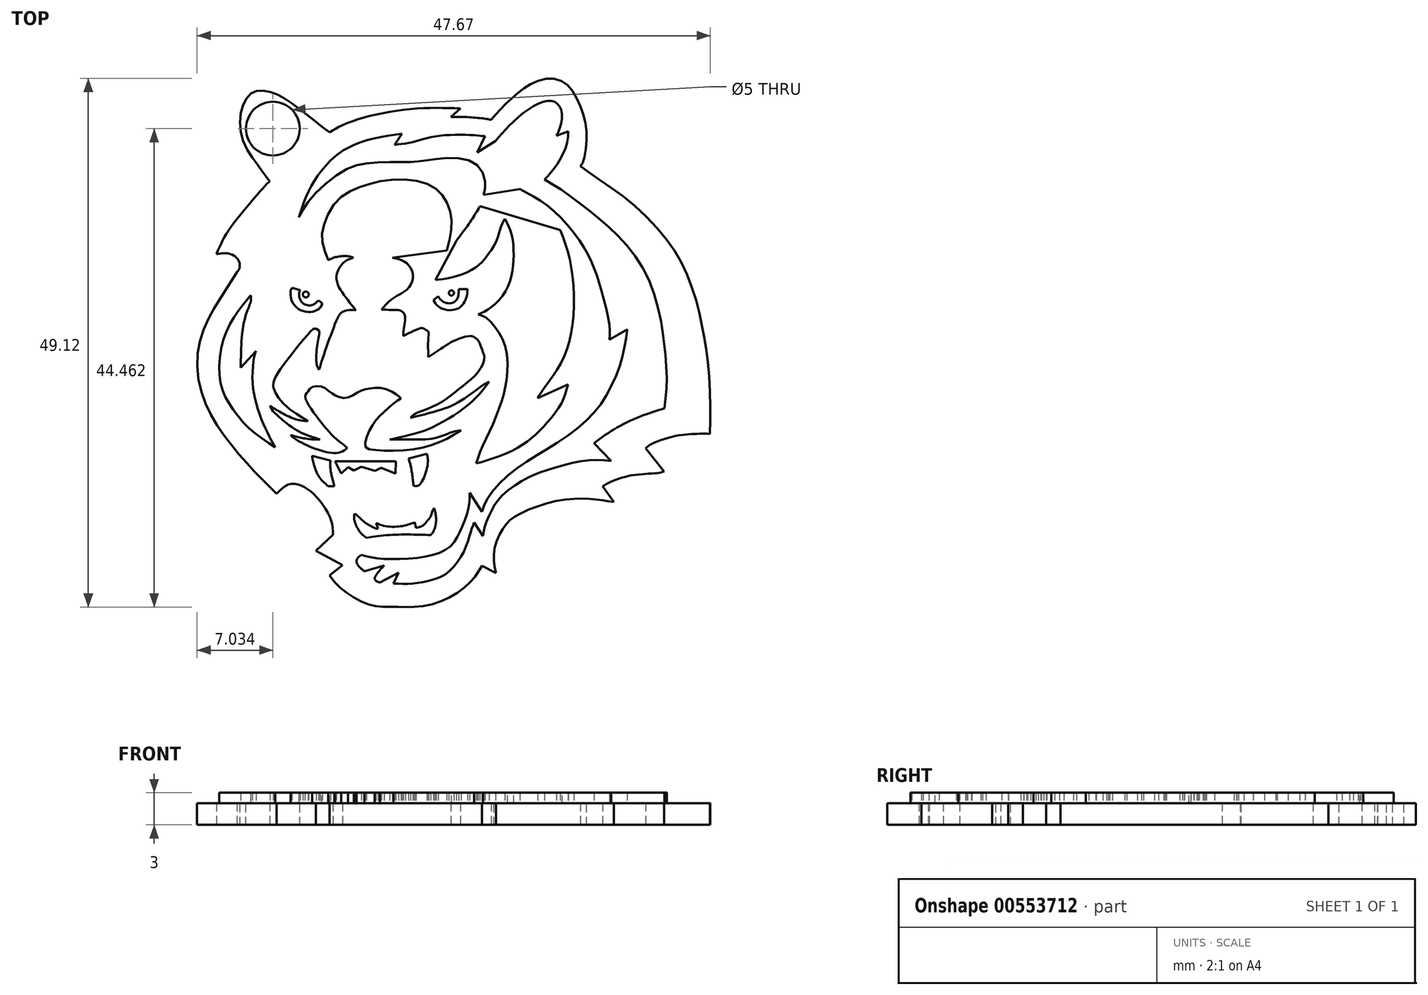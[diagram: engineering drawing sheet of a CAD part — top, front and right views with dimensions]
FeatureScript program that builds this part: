
annotation { "Feature Type Name" : "Feature", "Feature Type Description" : "" }
export const myFeature = defineFeature(function(context is Context, id is Id, definition is map)
    precondition{}
    {
        {
            var Q0;
            Q0=qCreatedBy(makeId("Top.planeOp"),FACE);
            var sketch = newSketch(context, id + "F0", { "sketchPlane" : qUnion([Q0])});
            skFitSpline(sketch, "E0", {"points": [v(7.81, 40.72) * mm, v(6.75, 42.15) * mm, v(5.2, 44.9) * mm, v(5.37, 47.9) * mm, v(6.45, 49.1) * mm, v(8.34, 48.86) * mm, v(10.63, 47.4) * mm, v(13.37, 45.26) * mm], "startDerivative": vector(-8.02, 10.82) * mm, "endDerivative": vector(16.53, -13.06) * mm});
            skFitSpline(sketch, "E1", {"points": [v(13.37, 45.26) * mm, v(14.48, 45.9) * mm, v(17.51, 46.9) * mm, v(21.92, 47.52) * mm, v(25.53, 47.5) * mm], "startDerivative": vector(5.91, 3.88) * mm, "endDerivative": vector(12.73, -0.45) * mm});
            skLineSegment(sketch, "E2", {"start": v(25.53, 47.5) * mm, "end": v(24.65, 46.7) * mm});
            skFitSpline(sketch, "E3", {"points": [v(24.65, 46.7) * mm, v(25.95, 46.7) * mm, v(27.64, 46.57) * mm, v(28.4, 46.44) * mm], "startDerivative": vector(3.55, 0.08) * mm, "endDerivative": vector(2.56, -0.49) * mm});
            skFitSpline(sketch, "E4", {"points": [v(28.4, 46.44) * mm, v(29.28, 47.45) * mm, v(30.65, 48.74) * mm, v(31.99, 49.72) * mm, v(33.8, 50.28) * mm, v(35.3, 49.8) * mm, v(36.35, 48.45) * mm, v(37.13, 46.27) * mm, v(37.24, 44.35) * mm, v(36.95, 42.59) * mm, v(36.68, 42.13) * mm], "startDerivative": vector(8.82, 10.83) * mm, "endDerivative": vector(-4.9, -6.26) * mm});
            skFitSpline(sketch, "E5", {"points": [v(36.68, 42.13) * mm, v(38.88, 40.57) * mm, v(41.72, 38.46) * mm, v(44.65, 35.36) * mm, v(46.27, 32.76) * mm, v(47.42, 29.68) * mm, v(48.02, 27.06) * mm, v(48.47, 24.4) * mm, v(48.73, 20.6) * mm, v(48.71, 17.26) * mm], "startDerivative": vector(21.07, -15.18) * mm, "endDerivative": vector(-0.6, -28.72) * mm});
            skFitSpline(sketch, "E6", {"points": [v(48.71, 17.26) * mm, v(47.43, 17.26) * mm, v(45.51, 17.05) * mm, v(43.32, 16.32) * mm, v(42.73, 15.9) * mm], "startDerivative": vector(-5.33, 0.08) * mm, "endDerivative": vector(-2.67, -2.33) * mm});
            skLineSegment(sketch, "E7", {"start": v(42.73, 15.9) * mm, "end": v(44.44, 13.75) * mm});
            skFitSpline(sketch, "E8", {"points": [v(44.44, 13.75) * mm, v(43.8, 13.6) * mm, v(41.83, 13.45) * mm, v(39.8, 12.93) * mm, v(38.74, 12.38) * mm], "startDerivative": vector(-3.21, -0.92) * mm, "endDerivative": vector(-4.23, -2.48) * mm});
            skLineSegment(sketch, "E9", {"start": v(38.74, 12.38) * mm, "end": v(39.77, 10.91) * mm});
            skFitSpline(sketch, "E10", {"points": [v(39.77, 10.91) * mm, v(38.01, 11.17) * mm, v(34.73, 11.07) * mm, v(30.8, 9.68) * mm, v(29.5, 8.5) * mm, v(28.66, 6.31) * mm, v(28.83, 4.33) * mm], "startDerivative": vector(-11.65, 2.05) * mm, "endDerivative": vector(2.66, -12.91) * mm});
            skLineSegment(sketch, "E11", {"start": v(28.83, 4.33) * mm, "end": v(27.53, 4.98) * mm});
            skFitSpline(sketch, "E12", {"points": [v(27.53, 4.98) * mm, v(26.17, 3.2) * mm, v(22.77, 1.4) * mm, v(19.43, 1.17) * mm, v(16.9, 1.44) * mm, v(14.23, 3.07) * mm, v(13.38, 4.11) * mm], "startDerivative": vector(-7.12, -11.85) * mm, "endDerivative": vector(-5.57, 8.3) * mm});
            skLineSegment(sketch, "E13", {"start": v(13.38, 4.11) * mm, "end": v(14.57, 5.06) * mm});
            skLineSegment(sketch, "E14", {"start": v(14.57, 5.06) * mm, "end": v(12.1, 6.37) * mm});
            skLineSegment(sketch, "E15", {"start": v(12.1, 6.37) * mm, "end": v(13.7, 7.88) * mm});
            skFitSpline(sketch, "E16", {"points": [v(13.7, 7.88) * mm, v(13.5, 9.24) * mm, v(12.24, 11.3) * mm, v(10.86, 12.38) * mm, v(9.66, 12.57) * mm, v(8.45, 11.69) * mm], "startDerivative": vector(-0.25, 6.98) * mm, "endDerivative": vector(-6.09, -5.97) * mm});
            skFitSpline(sketch, "E17", {"points": [v(8.45, 11.69) * mm, v(6.28, 13.88) * mm, v(3.78, 16.82) * mm, v(1.69, 20.46) * mm, v(1.15, 25) * mm, v(2.49, 28.64) * mm, v(3.74, 30.67) * mm, v(4.78, 32.28) * mm], "startDerivative": vector(-15.64, 15.32) * mm, "endDerivative": vector(9.41, 14.8) * mm});
            skFitSpline(sketch, "E18", {"points": [v(4.78, 32.28) * mm, v(5.04, 32.84) * mm, v(4.78, 33.57) * mm, v(3.95, 34.01) * mm, v(2.86, 33.96) * mm], "startDerivative": vector(1.64, 2.46) * mm, "endDerivative": vector(-3.9, -0.58) * mm});
            skFitSpline(sketch, "E19", {"points": [v(2.86, 33.96) * mm, v(3.74, 35.78) * mm, v(5.19, 37.75) * mm, v(7.28, 40.2) * mm, v(7.81, 40.72) * mm], "startDerivative": vector(3.23, 7.37) * mm, "endDerivative": vector(2.88, 2.61) * mm});
            skSolve(sketch);
        }
        {
            var Q0;
            Q0 = qSketchRegion(id + "F0", true);
            extrude(context, id + "F1", {"entities" : qUnion([Q0]), "depth" : 2 * mm, "offsetDistance" : 25 * mm});
        }
        {
            var Q0;
            Q0=makeQuery(id+"F1.opExtrude","CAP_FACE",FACE,{"disambiguationData":[OSD([sQuery(id+"F0.wireOp",EDGE,"E0"),sQuery(id+"F0.wireOp",EDGE,"E1"),sQuery(id+"F0.wireOp",EDGE,"E2"),sQuery(id+"F0.wireOp",EDGE,"E3"),sQuery(id+"F0.wireOp",EDGE,"E4"),sQuery(id+"F0.wireOp",EDGE,"E5"),sQuery(id+"F0.wireOp",EDGE,"E6"),sQuery(id+"F0.wireOp",EDGE,"E7"),sQuery(id+"F0.wireOp",EDGE,"E8"),sQuery(id+"F0.wireOp",EDGE,"E9"),sQuery(id+"F0.wireOp",EDGE,"E10"),sQuery(id+"F0.wireOp",EDGE,"E11"),sQuery(id+"F0.wireOp",EDGE,"E12"),sQuery(id+"F0.wireOp",EDGE,"E13"),sQuery(id+"F0.wireOp",EDGE,"E14"),sQuery(id+"F0.wireOp",EDGE,"E15"),sQuery(id+"F0.wireOp",EDGE,"E16"),sQuery(id+"F0.wireOp",EDGE,"E17"),sQuery(id+"F0.wireOp",EDGE,"E18"),sQuery(id+"F0.wireOp",EDGE,"E19")])],"isStart":false});
            var sketch = newSketch(context, id + "F2", { "sketchPlane" : qUnion([Q0])});
            skFitSpline(sketch, "E20", {"points": [v(10.53, 37.37) * mm, v(11.43, 39.82) * mm, v(13.3, 42.5) * mm, v(15.95, 44.25) * mm, v(20.1, 45.17) * mm], "startDerivative": vector(3.35, 10.9) * mm, "endDerivative": vector(15.52, 2.41) * mm});
            skLineSegment(sketch, "E21", {"start": v(20.1, 45.17) * mm, "end": v(19.39, 44.11) * mm});
            skFitSpline(sketch, "E22", {"points": [v(19.39, 44.11) * mm, v(21.18, 44.4) * mm, v(23.38, 44.94) * mm, v(26.66, 45.02) * mm, v(27.8, 44.92) * mm], "startDerivative": vector(7.65, 0.87) * mm, "endDerivative": vector(5.17, -0.57) * mm});
            skLineSegment(sketch, "E23", {"start": v(27.8, 44.92) * mm, "end": v(27.1, 43.4) * mm});
            skLineSegment(sketch, "E24", {"start": v(27.1, 43.4) * mm, "end": v(28.8, 44.48) * mm});
            skFitSpline(sketch, "E25", {"points": [v(28.8, 44.48) * mm, v(30.2, 46.04) * mm, v(32.48, 47.81) * mm, v(33.94, 48.2) * mm, v(34.71, 47.75) * mm, v(34.96, 46.42) * mm, v(34.45, 44.95) * mm], "startDerivative": vector(6.7, 8.1) * mm, "endDerivative": vector(-4.17, -8.84) * mm});
            skLineSegment(sketch, "E26", {"start": v(34.45, 44.95) * mm, "end": v(35.55, 45.38) * mm});
            skFitSpline(sketch, "E27", {"points": [v(35.55, 45.38) * mm, v(35.4, 44.18) * mm, v(34.5, 42.3) * mm, v(33.35, 40.9) * mm], "startDerivative": vector(-0.13, -4) * mm, "endDerivative": vector(-3.4, -3.76) * mm});
            skFitSpline(sketch, "E28", {"points": [v(33.35, 40.9) * mm, v(35.14, 39.77) * mm, v(37.76, 37.8) * mm, v(40.44, 35.37) * mm, v(42.85, 31.96) * mm, v(44.17, 27.69) * mm, v(44.55, 24.83) * mm, v(44.7, 21.88) * mm, v(44.48, 19.61) * mm], "startDerivative": vector(16.84, -9.97) * mm, "endDerivative": vector(-2.76, -20.54) * mm});
            skFitSpline(sketch, "E29", {"points": [v(44.48, 19.61) * mm, v(42.5, 18.97) * mm, v(40.03, 17.8) * mm, v(37.94, 16.4) * mm], "startDerivative": vector(-6.21, -1.84) * mm, "endDerivative": vector(-5.9, -4.31) * mm});
            skLineSegment(sketch, "E30", {"start": v(37.94, 16.4) * mm, "end": v(39.55, 14.75) * mm});
            skFitSpline(sketch, "E31", {"points": [v(39.55, 14.75) * mm, v(36.97, 14.75) * mm, v(33.68, 13.9) * mm, v(31.8, 13.18) * mm, v(29.49, 11.6) * mm, v(28.43, 10.14) * mm, v(27.8, 8.73) * mm, v(27.63, 7.76) * mm], "startDerivative": vector(-15.4, 1.2) * mm, "endDerivative": vector(-1.14, -9.47) * mm});
            skLineSegment(sketch, "E32", {"start": v(27.63, 7.76) * mm, "end": v(26.8, 9.02) * mm});
            skFitSpline(sketch, "E33", {"points": [v(26.8, 9.02) * mm, v(26.5, 8.2) * mm, v(25.9, 6.43) * mm, v(24.35, 4.37) * mm, v(22.78, 3.65) * mm, v(20.98, 3.34) * mm, v(19.3, 3.35) * mm], "startDerivative": vector(-2.47, -6.28) * mm, "endDerivative": vector(-10.06, 0.52) * mm});
            skLineSegment(sketch, "E34", {"start": v(19.3, 3.35) * mm, "end": v(19.8, 4.34) * mm});
            skLineSegment(sketch, "E35", {"start": v(19.8, 4.34) * mm, "end": v(18.02, 3.43) * mm});
            skFitSpline(sketch, "E36", {"points": [v(18.02, 3.43) * mm, v(17.66, 3.61) * mm, v(17.58, 3.88) * mm, v(18.45, 5.03) * mm], "startDerivative": vector(-1.53, 0.57) * mm, "endDerivative": vector(2.39, 2.61) * mm});
            skLineSegment(sketch, "E37", {"start": v(18.45, 5.03) * mm, "end": v(16.61, 4.49) * mm});
            skFitSpline(sketch, "E38", {"points": [v(16.61, 4.49) * mm, v(16.22, 4.81) * mm, v(15.87, 5.46) * mm, v(16.31, 6) * mm], "startDerivative": vector(-1.27, 0.92) * mm, "endDerivative": vector(1.85, 1.44) * mm});
            skFitSpline(sketch, "E39", {"points": [v(16.31, 6) * mm, v(18, 5.67) * mm, v(21.67, 5.75) * mm, v(24.4, 6.64) * mm, v(25.52, 8.24) * mm, v(26.25, 10.16) * mm, v(26.4, 11.79) * mm], "startDerivative": vector(10.26, -2.68) * mm, "endDerivative": vector(0.23, 11.3) * mm});
            skLineSegment(sketch, "E40", {"start": v(26.4, 11.79) * mm, "end": v(27.54, 10.01) * mm});
            skFitSpline(sketch, "E41", {"points": [v(27.54, 10.01) * mm, v(28.07, 11.31) * mm, v(30.5, 13.84) * mm, v(34.06, 16.13) * mm, v(37.5, 18.76) * mm, v(39.42, 21.42) * mm, v(40.62, 24.55) * mm, v(41.01, 26.96) * mm], "startDerivative": vector(3.56, 12.77) * mm, "endDerivative": vector(2.1, 18.49) * mm});
            skLineSegment(sketch, "E42", {"start": v(41.01, 26.96) * mm, "end": v(39.37, 26) * mm});
            skFitSpline(sketch, "E43", {"points": [v(39.37, 26) * mm, v(39.37, 27.44) * mm, v(38.38, 31.39) * mm, v(37.18, 34.28) * mm, v(34.1, 38.06) * mm, v(31.05, 40) * mm], "startDerivative": vector(0.9, 9.34) * mm, "endDerivative": vector(-14.64, 7.54) * mm});
            skFitSpline(sketch, "E44", {"points": [v(10.53, 37.37) * mm, v(11.64, 39.14) * mm, v(14.84, 41.79) * mm, v(17.34, 42.45) * mm, v(20.51, 42.52) * mm, v(22.04, 42.63) * mm, v(24.67, 42.9) * mm, v(27.07, 42.26) * mm, v(27.83, 40.57) * mm, v(27.68, 39.48) * mm], "startDerivative": vector(8, 15.77) * mm, "endDerivative": vector(-3.48, -13.06) * mm});
            skLineSegment(sketch, "E45", {"start": v(31.05, 40) * mm, "end": v(27.68, 39.48) * mm});
            skSolve(sketch);
        }
        {
            var Q0;
            Q0 = qSketchRegion(id + "F2", true);
            extrude(context, id + "F3", {"entities" : qUnion([Q0]), "operationType" : NewBodyOperationType.ADD, "depth" : 1 * mm, "offsetDistance" : 25 * mm});
        }
        {
            var Q0;
            Q0=makeQuery(id+"F1.opExtrude","CAP_FACE",FACE,{"disambiguationData":[OSD([sQuery(id+"F0.wireOp",EDGE,"E0"),sQuery(id+"F0.wireOp",EDGE,"E1"),sQuery(id+"F0.wireOp",EDGE,"E2"),sQuery(id+"F0.wireOp",EDGE,"E3"),sQuery(id+"F0.wireOp",EDGE,"E4"),sQuery(id+"F0.wireOp",EDGE,"E5"),sQuery(id+"F0.wireOp",EDGE,"E6"),sQuery(id+"F0.wireOp",EDGE,"E7"),sQuery(id+"F0.wireOp",EDGE,"E8"),sQuery(id+"F0.wireOp",EDGE,"E9"),sQuery(id+"F0.wireOp",EDGE,"E10"),sQuery(id+"F0.wireOp",EDGE,"E11"),sQuery(id+"F0.wireOp",EDGE,"E12"),sQuery(id+"F0.wireOp",EDGE,"E13"),sQuery(id+"F0.wireOp",EDGE,"E14"),sQuery(id+"F0.wireOp",EDGE,"E15"),sQuery(id+"F0.wireOp",EDGE,"E16"),sQuery(id+"F0.wireOp",EDGE,"E17"),sQuery(id+"F0.wireOp",EDGE,"E18"),sQuery(id+"F0.wireOp",EDGE,"E19")])],"isStart":false});
            var sketch = newSketch(context, id + "F4", { "sketchPlane" : qUnion([Q0])});
            skCircle(sketch, "E46", {"center": v(8.1, 45.62) * mm, "radius": 2.5 * mm});
            skSolve(sketch);
        }
        {
            var Q0;
            Q0 = qSketchRegion(id + "F4", true);
            extrude(context, id + "F5", {"entities" : qUnion([Q0]), "operationType" : NewBodyOperationType.REMOVE, "oppositeDirection" : true, "depth" : 9.3 * mm, "offsetDistance" : 25 * mm});
        }
        {
            var Q0;
            Q0=qCreatedBy(makeId("Top.planeOp"),FACE);
            var sketch = newSketch(context, id + "F6", { "sketchPlane" : qUnion([Q0])});
            skFitSpline(sketch, "E47", {"points": [v(13.24, 33.4) * mm, v(12.68, 35.22) * mm, v(12.9, 36.85) * mm, v(14.22, 39.08) * mm, v(16.26, 40.21) * mm, v(18.57, 40.82) * mm, v(21.75, 40.71) * mm, v(23.6, 39.73) * mm, v(24.47, 38.23) * mm, v(24.71, 36.58) * mm, v(24.27, 34.3) * mm], "startDerivative": vector(-7.82, 19.9) * mm, "endDerivative": vector(-5.93, -22.88) * mm});
            skFitSpline(sketch, "E48", {"points": [v(13.24, 33.4) * mm, v(13.75, 33.63) * mm, v(14.83, 33.8) * mm, v(15.59, 33.65) * mm], "startDerivative": vector(1.6, 0.86) * mm, "endDerivative": vector(2.13, -0.64) * mm});
            skFitSpline(sketch, "E49", {"points": [v(15.59, 33.65) * mm, v(15, 33.4) * mm, v(14.33, 32.77) * mm, v(14.01, 31.8) * mm, v(14.3, 30.8) * mm, v(15.01, 29.75) * mm, v(15.81, 28.75) * mm], "startDerivative": vector(-4.44, -1.5) * mm, "endDerivative": vector(4.26, -5.28) * mm});
            skFitSpline(sketch, "E50", {"points": [v(15.81, 28.75) * mm, v(15.14, 28.75) * mm, v(14.4, 28.45) * mm, v(13.83, 27.34) * mm, v(13.09, 25.32) * mm, v(12.4, 23.22) * mm], "startDerivative": vector(-4.6, 0.29) * mm, "endDerivative": vector(-2.56, -8.11) * mm});
            skFitSpline(sketch, "E51", {"points": [v(12.4, 23.22) * mm, v(12.21, 23.56) * mm, v(12.14, 24.15) * mm, v(12.23, 25.5) * mm, v(12.4, 26.45) * mm, v(12.4, 26.86) * mm], "startDerivative": vector(-1.43, 2.12) * mm, "endDerivative": vector(-0.16, 2.44) * mm});
            skFitSpline(sketch, "E52", {"points": [v(12.4, 26.86) * mm, v(11.97, 27.06) * mm, v(11.42, 26.58) * mm, v(10.45, 25.41) * mm, v(9.17, 23.78) * mm, v(8.43, 22.68) * mm, v(8.13, 21.72) * mm, v(9.2, 19.96) * mm, v(11.08, 18.62) * mm, v(11.36, 18.46) * mm], "startDerivative": vector(-6.12, 4.78) * mm, "endDerivative": vector(3.63, -2.2) * mm});
            skFitSpline(sketch, "E53", {"points": [v(11.36, 18.46) * mm, v(10.33, 18.58) * mm, v(8.78, 19.29) * mm, v(7.83, 19.88) * mm], "startDerivative": vector(-3.22, 0.09) * mm, "endDerivative": vector(-2.75, 1.81) * mm});
            skFitSpline(sketch, "E54", {"points": [v(7.83, 19.88) * mm, v(8.02, 19.5) * mm, v(9.4, 18.23) * mm, v(10.93, 17.27) * mm, v(12.5, 16.73) * mm], "startDerivative": vector(0.74, -2.41) * mm, "endDerivative": vector(5.78, -1.73) * mm});
            skFitSpline(sketch, "E55", {"points": [v(12.5, 16.73) * mm, v(12, 16.73) * mm, v(10.66, 16.9) * mm, v(9.75, 17.15) * mm], "startDerivative": vector(-1.73, -0.07) * mm, "endDerivative": vector(-2.4, 0.78) * mm});
            skFitSpline(sketch, "E56", {"points": [v(9.75, 17.15) * mm, v(10.06, 16.86) * mm, v(11.59, 16.05) * mm, v(13.5, 15.48) * mm, v(14.46, 15.58) * mm, v(15.01, 15.94) * mm], "startDerivative": vector(1.88, -2.12) * mm, "endDerivative": vector(3.25, 2.62) * mm});
            skFitSpline(sketch, "E57", {"points": [v(15.01, 15.94) * mm, v(14.5, 16.37) * mm, v(13.6, 17.15) * mm, v(12.1, 18.98) * mm, v(11.1, 20.72) * mm, v(11.36, 21.18) * mm], "startDerivative": vector(-3.23, 2.86) * mm, "endDerivative": vector(3.01, 2.95) * mm});
            skFitSpline(sketch, "E58", {"points": [v(11.36, 21.18) * mm, v(11.7, 21.57) * mm, v(12.62, 21.65) * mm, v(13.37, 21.18) * mm, v(14.11, 20.72) * mm, v(15.01, 20.63) * mm, v(16.15, 21.18) * mm, v(17.02, 21.46) * mm, v(18.45, 21.47) * mm, v(19.73, 20.79) * mm, v(20, 20.54) * mm], "startDerivative": vector(3.35, 5.85) * mm, "endDerivative": vector(3.17, -3.45) * mm});
            skFitSpline(sketch, "E59", {"points": [v(20, 20.54) * mm, v(19.56, 20.26) * mm, v(18.59, 19.44) * mm, v(17.83, 18.7) * mm, v(17.12, 17.64) * mm, v(16.67, 16.32) * mm, v(16.81, 15.94) * mm, v(18.1, 15.71) * mm, v(21.06, 15.8) * mm, v(23.65, 16.5) * mm, v(25.6, 17.57) * mm], "startDerivative": vector(-6.46, -3.6) * mm, "endDerivative": vector(14.8, 8.97) * mm});
            skFitSpline(sketch, "E60", {"points": [v(25.6, 17.57) * mm, v(24.85, 17.44) * mm, v(23.25, 16.88) * mm, v(21.21, 16.73) * mm, v(18.95, 16.73) * mm], "startDerivative": vector(-4.02, -0.33) * mm, "endDerivative": vector(-7.75, -0.01) * mm});
            skFitSpline(sketch, "E61", {"points": [v(18.95, 16.73) * mm, v(19.57, 16.86) * mm, v(21.39, 17.3) * mm, v(22.95, 17.89) * mm, v(25.2, 19.16) * mm, v(26.9, 20.54) * mm, v(28.2, 22.1) * mm], "startDerivative": vector(5.26, 1.04) * mm, "endDerivative": vector(6.92, 9.02) * mm});
            skFitSpline(sketch, "E62", {"points": [v(28.2, 22.1) * mm, v(27.55, 21.72) * mm, v(25.6, 20.35) * mm, v(23.78, 19.52) * mm, v(20.91, 18.75) * mm], "startDerivative": vector(-3.56, -1.81) * mm, "endDerivative": vector(-9.88, -2.45) * mm});
            skFitSpline(sketch, "E63", {"points": [v(20.91, 18.75) * mm, v(21.28, 19.08) * mm, v(23.36, 19.97) * mm, v(25.44, 21.46) * mm, v(27.2, 23.02) * mm, v(27.76, 24.31) * mm, v(27.63, 24.79) * mm], "startDerivative": vector(2.67, 3.37) * mm, "endDerivative": vector(-2.1, 4.28) * mm});
            skFitSpline(sketch, "E64", {"points": [v(27.63, 24.79) * mm, v(27.32, 25.68) * mm, v(26.72, 26.3) * mm, v(25.8, 26.23) * mm, v(24.7, 25.8) * mm, v(23.84, 25.24) * mm, v(22.54, 24.4) * mm], "startDerivative": vector(-1.62, 5.77) * mm, "endDerivative": vector(-6.9, -4.43) * mm});
            skFitSpline(sketch, "E65", {"points": [v(22.54, 24.4) * mm, v(22.54, 25.04) * mm, v(22.54, 25.97) * mm, v(22.54, 26.78) * mm, v(22.32, 26.92) * mm, v(21.98, 27.08) * mm, v(21.27, 26.86) * mm, v(20.22, 26.37) * mm], "startDerivative": vector(0.05, 4.46) * mm, "endDerivative": vector(-5.69, -2.7) * mm});
            skFitSpline(sketch, "E66", {"points": [v(20.22, 26.37) * mm, v(20.22, 26.74) * mm, v(20.36, 27.61) * mm, v(20.36, 28.28) * mm, v(19.99, 28.7) * mm, v(19.33, 28.78) * mm, v(18.19, 28.8) * mm], "startDerivative": vector(-0.17, 2.7) * mm, "endDerivative": vector(-5.67, 0.14) * mm});
            skFitSpline(sketch, "E67", {"points": [v(18.19, 28.8) * mm, v(19.3, 29.86) * mm, v(20.74, 30.85) * mm, v(21.1, 32.16) * mm, v(20.36, 33.24) * mm, v(19.22, 33.62) * mm], "startDerivative": vector(4.77, 5.48) * mm, "endDerivative": vector(-6.56, 1.2) * mm});
            skLineSegment(sketch, "E68", {"start": v(24.27, 34.3) * mm, "end": v(19.22, 33.62) * mm});
            skSolve(sketch);
        }
        {
            var Q0;
            Q0 = qSketchRegion(id + "F6", true);
            extrude(context, id + "F7", {"entities" : qUnion([Q0]), "operationType" : NewBodyOperationType.ADD, "depth" : 3 * mm, "offsetDistance" : 25 * mm});
        }
        {
            var Q0;
            Q0=qCreatedBy(makeId("Top.planeOp"),FACE);
            var sketch = newSketch(context, id + "F8", { "sketchPlane" : qUnion([Q0])});
            skLineSegment(sketch, "E69", {"start": v(11.75, 15.2) * mm, "end": v(13.46, 14.78) * mm});
            skFitSpline(sketch, "E70", {"points": [v(11.75, 15.2) * mm, v(11.88, 14.54) * mm, v(12.36, 13.32) * mm, v(13.24, 12.4) * mm], "startDerivative": vector(0.37, -2.26) * mm, "endDerivative": vector(2.65, -2.27) * mm});
            skLineSegment(sketch, "E71", {"start": v(13.24, 12.4) * mm, "end": v(13.81, 12.4) * mm});
            skFitSpline(sketch, "E72", {"points": [v(13.46, 14.78) * mm, v(13.46, 13.93) * mm, v(13.81, 12.4) * mm], "startDerivative": vector(-0.13, -1.86) * mm, "endDerivative": vector(0.79, -2.86) * mm});
            skLineSegment(sketch, "E73", {"start": v(13.88, 14.7) * mm, "end": v(19.52, 14.7) * mm});
            skLineSegment(sketch, "E74", {"start": v(13.88, 14.7) * mm, "end": v(14.46, 13.57) * mm});
            skLineSegment(sketch, "E75", {"start": v(14.46, 13.57) * mm, "end": v(15.08, 14.17) * mm});
            skLineSegment(sketch, "E76", {"start": v(15.08, 14.17) * mm, "end": v(15.62, 13.85) * mm});
            skLineSegment(sketch, "E77", {"start": v(15.62, 13.85) * mm, "end": v(16.33, 14.2) * mm});
            skLineSegment(sketch, "E78", {"start": v(16.33, 14.2) * mm, "end": v(17.58, 13.82) * mm});
            skLineSegment(sketch, "E79", {"start": v(17.58, 13.82) * mm, "end": v(18.16, 14.1) * mm});
            skLineSegment(sketch, "E80", {"start": v(18.16, 14.1) * mm, "end": v(19.49, 13.57) * mm});
            skLineSegment(sketch, "E81", {"start": v(19.49, 13.57) * mm, "end": v(19.52, 14.7) * mm});
            skLineSegment(sketch, "E82", {"start": v(20.7, 14.95) * mm, "end": v(22.44, 15.41) * mm});
            skFitSpline(sketch, "E83", {"points": [v(20.7, 14.95) * mm, v(20.93, 14.18) * mm, v(21.18, 12.43) * mm], "startDerivative": vector(0.58, -1.72) * mm, "endDerivative": vector(0.37, -3.23) * mm});
            skFitSpline(sketch, "E84", {"points": [v(21.18, 12.43) * mm, v(21.6, 12.43) * mm, v(22.08, 13.06) * mm, v(22.5, 14.5) * mm, v(22.44, 15.41) * mm], "startDerivative": vector(2.44, -0.49) * mm, "endDerivative": vector(-0.53, 3.29) * mm});
            skFitSpline(sketch, "E85", {"points": [v(15.7, 9.85) * mm, v(15.67, 9.27) * mm, v(16.17, 8.17) * mm, v(16.8, 7.58) * mm], "startDerivative": vector(-0.36, -1.91) * mm, "endDerivative": vector(1.93, -1.45) * mm});
            skFitSpline(sketch, "E86", {"points": [v(16.8, 7.58) * mm, v(17.53, 7.7) * mm, v(18.8, 7.84) * mm, v(20.16, 7.9) * mm, v(21.6, 7.88) * mm, v(22.77, 7.85) * mm], "startDerivative": vector(4.28, 0.73) * mm, "endDerivative": vector(5.74, -0.17) * mm});
            skFitSpline(sketch, "E87", {"points": [v(22.77, 7.85) * mm, v(23.07, 8.27) * mm, v(23.27, 9.41) * mm, v(23.08, 10.34) * mm], "startDerivative": vector(1.23, 1.33) * mm, "endDerivative": vector(-0.74, 2.47) * mm});
            skFitSpline(sketch, "E88", {"points": [v(23.08, 10.34) * mm, v(22.9, 10.04) * mm, v(22.78, 9.6) * mm, v(22.47, 9.2) * mm, v(22.11, 8.79) * mm, v(21.63, 8.56) * mm, v(21.4, 8.52) * mm], "startDerivative": vector(-1.4, -1.82) * mm, "endDerivative": vector(-1.68, -0.2) * mm});
            skFitSpline(sketch, "E89", {"points": [v(21.4, 8.52) * mm, v(21.27, 9.04) * mm], "startDerivative": vector(-0.13, 0.51) * mm, "endDerivative": vector(-0.13, 0.51) * mm});
            skFitSpline(sketch, "E90", {"points": [v(21.27, 9.04) * mm, v(21, 8.93) * mm, v(20.42, 8.75) * mm, v(19.96, 8.66) * mm, v(19.02, 8.62) * mm, v(18.13, 8.79) * mm, v(17.7, 8.97) * mm], "startDerivative": vector(-1.93, -0.9) * mm, "endDerivative": vector(-2.58, 1.28) * mm});
            skFitSpline(sketch, "E91", {"points": [v(17.7, 8.97) * mm, v(17.88, 8.45) * mm], "startDerivative": vector(0.17, -0.52) * mm, "endDerivative": vector(0.17, -0.52) * mm});
            skFitSpline(sketch, "E92", {"points": [v(17.88, 8.45) * mm, v(17.7, 8.45) * mm, v(17.25, 8.67) * mm, v(16.63, 9.04) * mm, v(16.04, 9.58) * mm, v(15.7, 9.85) * mm], "startDerivative": vector(-1.34, -0.22) * mm, "endDerivative": vector(-1.76, 1.26) * mm});
            skSolve(sketch);
        }
        {
            var Q0;
            Q0 = qSketchRegion(id + "F8", true);
            extrude(context, id + "F9", {"entities" : qUnion([Q0]), "operationType" : NewBodyOperationType.ADD, "depth" : 3 * mm, "offsetDistance" : 25 * mm});
        }
        {
            var Q0;
            Q0=qCreatedBy(makeId("Top.planeOp"),FACE);
            var sketch = newSketch(context, id + "F10", { "sketchPlane" : qUnion([Q0])});
            skCircle(sketch, "E93", {"center": v(11.17, 30.2) * mm, "radius": 0.27 * mm});
            skCircle(sketch, "E94", {"center": v(24.7, 30.35) * mm, "radius": 0.24 * mm});
            skLineSegment(sketch, "E95", {"start": v(9.86, 30.82) * mm, "end": v(10.63, 30.6) * mm});
            skFitSpline(sketch, "E96", {"points": [v(10.63, 30.6) * mm, v(10.54, 30.08) * mm, v(10.8, 29.5) * mm, v(11.3, 29.21) * mm, v(11.82, 29.25) * mm, v(12.34, 29.65) * mm], "startDerivative": vector(-0.82, -2.67) * mm, "endDerivative": vector(2.38, 2.29) * mm});
            skLineSegment(sketch, "E97", {"start": v(12.34, 29.65) * mm, "end": v(12.7, 29.38) * mm});
            skFitSpline(sketch, "E98", {"points": [v(9.86, 30.82) * mm, v(9.75, 30.52) * mm, v(9.86, 29.64) * mm, v(10.25, 29.04) * mm, v(10.9, 28.67) * mm, v(11.8, 28.6) * mm, v(12.41, 28.91) * mm, v(12.7, 29.38) * mm], "startDerivative": vector(-1.51, -2.47) * mm, "endDerivative": vector(1.87, 3.84) * mm});
            skLineSegment(sketch, "E99", {"start": v(25.37, 30.7) * mm, "end": v(26.18, 30.7) * mm});
            skLineSegment(sketch, "E100", {"start": v(23.46, 30.04) * mm, "end": v(23.03, 29.67) * mm});
            skFitSpline(sketch, "E101", {"points": [v(23.03, 29.67) * mm, v(23.36, 29.21) * mm, v(24.07, 28.81) * mm, v(25.1, 28.82) * mm, v(25.74, 29.27) * mm, v(26.1, 30) * mm, v(26.18, 30.7) * mm], "startDerivative": vector(1.93, -3.38) * mm, "endDerivative": vector(0.25, 4.38) * mm});
            skFitSpline(sketch, "E102", {"points": [v(23.46, 30.04) * mm, v(23.74, 29.67) * mm, v(24.13, 29.45) * mm, v(24.7, 29.4) * mm, v(25.15, 29.67) * mm, v(25.32, 30.04) * mm, v(25.37, 30.7) * mm], "startDerivative": vector(1.67, -2.47) * mm, "endDerivative": vector(0.08, 3.7) * mm});
            skSolve(sketch);
        }
        {
            var Q0;
            Q0 = qSketchRegion(id + "F10", true);
            extrude(context, id + "F11", {"entities" : qUnion([Q0]), "operationType" : NewBodyOperationType.ADD, "depth" : 3 * mm, "offsetDistance" : 25 * mm});
        }
        {
            var Q0;
            Q0=qCreatedBy(makeId("Top.planeOp"),FACE);
            var sketch = newSketch(context, id + "F12", { "sketchPlane" : qUnion([Q0])});
            skFitSpline(sketch, "E103", {"points": [v(6.05, 30.13) * mm, v(4.71, 28.43) * mm, v(3.44, 25.78) * mm, v(3.19, 22.26) * mm, v(4.08, 20) * mm, v(5.9, 17.79) * mm, v(8.33, 16) * mm], "startDerivative": vector(-9.3, -10.95) * mm, "endDerivative": vector(14.69, -9.59) * mm});
            skFitSpline(sketch, "E104", {"points": [v(8.33, 16) * mm, v(7.83, 16.9) * mm, v(6.86, 19.11) * mm, v(6.22, 22.03) * mm, v(6.39, 24.53) * mm, v(6.54, 24.97) * mm], "startDerivative": vector(-3.01, 5.17) * mm, "endDerivative": vector(1.5, 3.21) * mm});
            skFitSpline(sketch, "E105", {"points": [v(6.05, 30.13) * mm, v(6.05, 29.6) * mm, v(5.6, 28.32) * mm, v(5.2, 25.96) * mm, v(5.12, 23.42) * mm], "startDerivative": vector(0.43, -3.4) * mm, "endDerivative": vector(-0.09, -8) * mm});
            skLineSegment(sketch, "E106", {"start": v(6.54, 24.97) * mm, "end": v(5.12, 23.42) * mm});
            skFitSpline(sketch, "E107", {"points": [v(35.53, 21.84) * mm, v(34.99, 20.24) * mm, v(33.53, 18.22) * mm, v(31.97, 16.72) * mm, v(29.82, 15.44) * mm, v(27.19, 14.55) * mm, v(27, 14.5) * mm], "startDerivative": vector(-2.4, -9.68) * mm, "endDerivative": vector(-2.42, -0.34) * mm});
            skFitSpline(sketch, "E108", {"points": [v(27, 14.5) * mm, v(27.53, 16) * mm, v(28.46, 17.97) * mm, v(29.4, 20.42) * mm, v(29.82, 22.34) * mm, v(29.78, 25.1) * mm, v(28.87, 27.02) * mm, v(27.87, 28.09) * mm, v(27.19, 28.34) * mm], "startDerivative": vector(4.18, 12.67) * mm, "endDerivative": vector(-8.59, 2.08) * mm});
            skFitSpline(sketch, "E109", {"points": [v(27.19, 28.34) * mm, v(28, 28.78) * mm, v(29.4, 30.02) * mm, v(30.3, 32.02) * mm, v(30.47, 34.07) * mm, v(30.24, 35.99) * mm, v(29.64, 37.25) * mm], "startDerivative": vector(6.2, 2.92) * mm, "endDerivative": vector(-4.46, 7.8) * mm});
            skFitSpline(sketch, "E110", {"points": [v(29.64, 37.25) * mm, v(29.37, 36.7) * mm, v(28.87, 35.18) * mm, v(28.04, 33.85) * mm, v(27.41, 33.1) * mm, v(26.13, 32.25) * mm, v(24.15, 31.68) * mm, v(23.2, 31.56) * mm], "startDerivative": vector(-2.86, -4.73) * mm, "endDerivative": vector(-6.88, -0.61) * mm});
            skLineSegment(sketch, "E111", {"start": v(23.2, 31.56) * mm, "end": v(25.14, 35.17) * mm});
            skLineSegment(sketch, "E112", {"start": v(35.53, 21.84) * mm, "end": v(32.7, 20.56) * mm});
            skFitSpline(sketch, "E113", {"points": [v(32.7, 20.56) * mm, v(33.23, 21.4) * mm, v(34.89, 23.87) * mm, v(35.97, 27.57) * mm, v(35.82, 32.84) * mm, v(34.8, 36.2) * mm], "startDerivative": vector(3.86, 6.5) * mm, "endDerivative": vector(-5.53, 14.57) * mm});
            skFitSpline(sketch, "E114", {"points": [v(25.14, 35.17) * mm, v(25.47, 35.63) * mm, v(26.4, 36.88) * mm, v(27.33, 38.4) * mm], "startDerivative": vector(1.22, 1.82) * mm, "endDerivative": vector(2.18, 3.83) * mm});
            skLineSegment(sketch, "E115", {"start": v(34.8, 36.2) * mm, "end": v(27.33, 38.4) * mm});
            skSolve(sketch);
        }
        {
            var Q0;
            Q0 = qSketchRegion(id + "F12", true);
            extrude(context, id + "F13", {"entities" : qUnion([Q0]), "operationType" : NewBodyOperationType.ADD, "depth" : 3 * mm, "offsetDistance" : 25 * mm});
        }
    });
